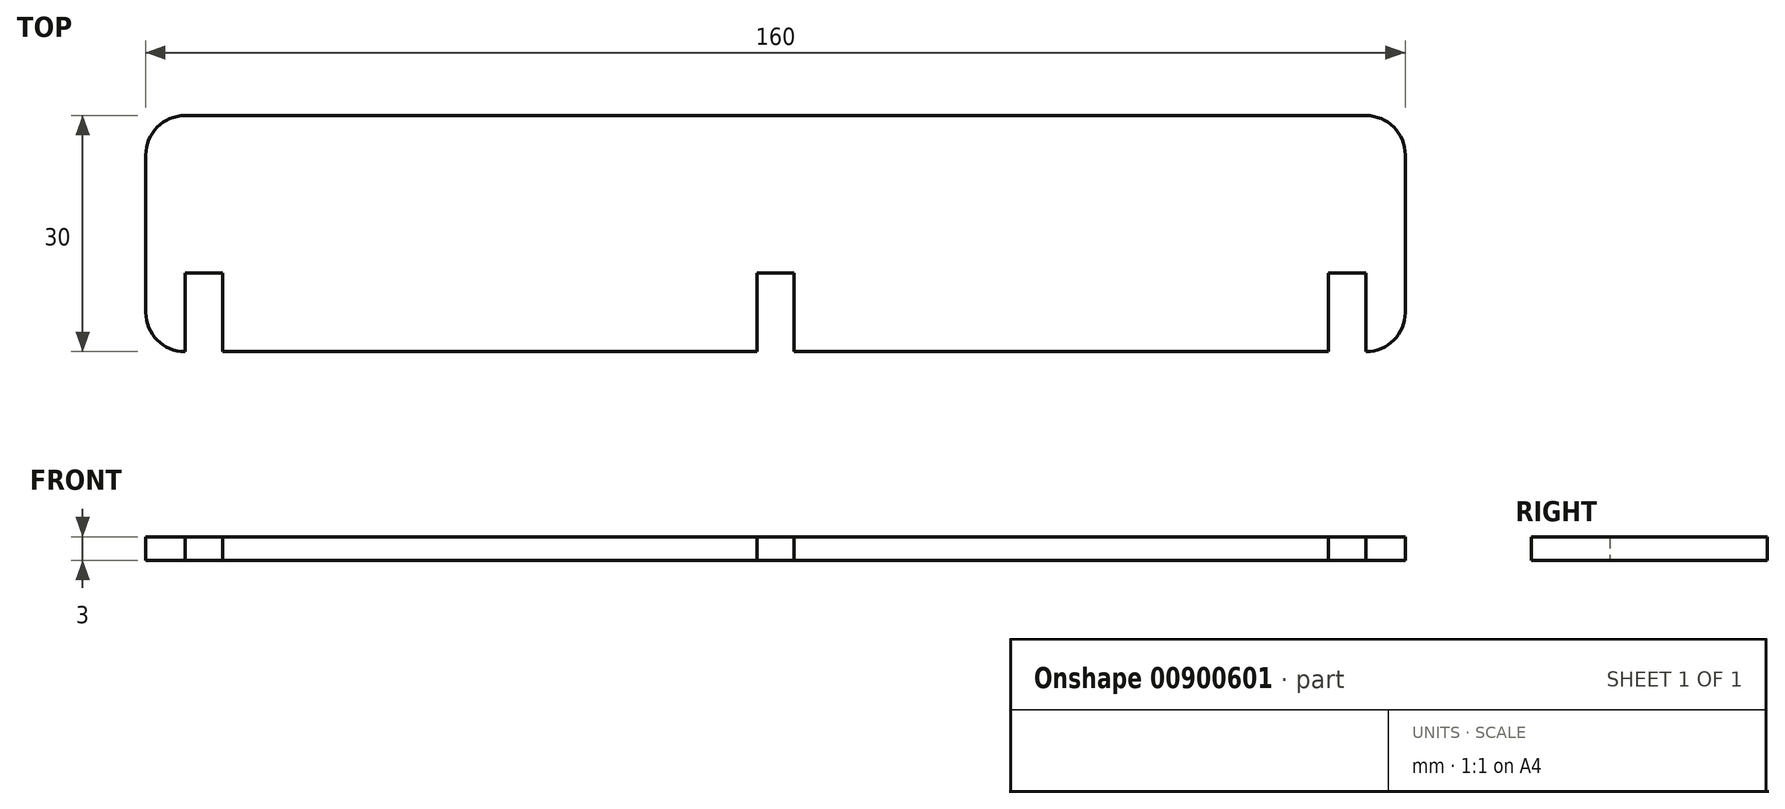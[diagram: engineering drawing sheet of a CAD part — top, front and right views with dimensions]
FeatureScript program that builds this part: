
annotation { "Feature Type Name" : "Feature", "Feature Type Description" : "" }
export const myFeature = defineFeature(function(context is Context, id is Id, definition is map)
    precondition{}
    {
        {
            var Q0;
            Q0=qCreatedBy(makeId("Top.planeOp"),FACE);
            var sketch = newSketch(context, id + "F0", { "sketchPlane" : qUnion([Q0])});
            skLineSegment(sketch, "E0.bottom", {"start": v(-75, 15) * mm, "end": v(75, 15) * mm});
            skLineSegment(sketch, "E0.top", {"start": v(-75, -15) * mm, "end": v(75, -15) * mm});
            skLineSegment(sketch, "E0.left", {"start": v(-80, 10) * mm, "end": v(-80, -10) * mm});
            skLineSegment(sketch, "E0.right", {"start": v(80, 10) * mm, "end": v(80, -10) * mm});
            skPoint(sketch, "E0.middle", {"position": v(0, 0) * mm});
            skPoint(sketch, "E1", {"position": v(-75, -15) * mm});
            skPoint(sketch, "E2", {"position": v(0, -15) * mm});
            skPoint(sketch, "E3", {"position": v(75, -15) * mm});
            skLineSegment(sketch, "E4", {"start": v(-75, -15) * mm, "end": v(-75, -5) * mm});
            skLineSegment(sketch, "E5", {"start": v(-75, -5) * mm, "end": v(-70.25, -5) * mm});
            skLineSegment(sketch, "E6", {"start": v(-70.25, -5) * mm, "end": v(-70.25, -15) * mm});
            skLineSegment(sketch, "E7", {"start": v(-75, -15) * mm, "end": v(-70.25, -15) * mm});
            skLineSegment(sketch, "E8.1.0.0", {"start": v(2.38, -5) * mm, "end": v(2.38, -15) * mm});
            skLineSegment(sketch, "E8.1.0.1", {"start": v(-2.38, -5) * mm, "end": v(2.37, -5) * mm});
            skLineSegment(sketch, "E8.1.0.2", {"start": v(-2.37, -15) * mm, "end": v(-2.37, -5) * mm});
            skLineSegment(sketch, "E8.2.0.0", {"start": v(75, -5) * mm, "end": v(75, -15) * mm});
            skLineSegment(sketch, "E8.2.0.1", {"start": v(70.25, -5) * mm, "end": v(75, -5) * mm});
            skLineSegment(sketch, "E8.2.0.2", {"start": v(70.25, -15) * mm, "end": v(70.25, -5) * mm});
            skLineSegment(sketch, "E8.direction1", {"start": v(-75, -15) * mm, "end": v(-2.38, -15) * mm, "construction": true});
            skPoint(sketch, "E9.visualSharp", {"position": v(-80, -15) * mm});
            skArc(sketch, "E9.filletArc", {"start": v(-80, -10) * mm, "mid": v(-78.54, -13.54) * mm, "end": v(-75, -15) * mm});
            skPoint(sketch, "E10.visualSharp", {"position": v(80, -15) * mm});
            skArc(sketch, "E10.filletArc", {"start": v(75, -15) * mm, "mid": v(78.54, -13.54) * mm, "end": v(80, -10) * mm});
            skPoint(sketch, "E11.visualSharp", {"position": v(-80, 15) * mm});
            skArc(sketch, "E11.filletArc", {"start": v(-75, 15) * mm, "mid": v(-78.54, 13.54) * mm, "end": v(-80, 10) * mm});
            skPoint(sketch, "E12.visualSharp", {"position": v(80, 15) * mm});
            skArc(sketch, "E12.filletArc", {"start": v(80, 10) * mm, "mid": v(78.54, 13.54) * mm, "end": v(75, 15) * mm});
            skSolve(sketch);
        }
        {
            var Q0;
            Q0=makeQuery(id+"F0.imprint","IMPRINT",FACE,{"disambiguationData":[TD([[makeQuery(id+"F0.imprint","IMPRINT",EDGE,{"derivedFrom":sQuery(id+"F0.wireOp",EDGE,"E0.bottom")}),-1.0]])]});
            extrude(context, id + "F1", {"entities" : qUnion([Q0]), "depth" : 3 * mm, "offsetDistance" : 25 * mm});
        }
    });
